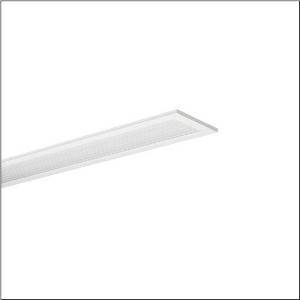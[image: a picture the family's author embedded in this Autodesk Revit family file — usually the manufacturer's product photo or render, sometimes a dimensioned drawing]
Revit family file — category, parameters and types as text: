
# Revit family: apollon_21_linear_51mq15wd2414
name_source: partatom
category: Lighting Fixtures
units: mm (PartAtom-declared; Revit-internal decimal feet)

## family parameters
Cut with Voids When Loaded = No
Host = Face
Light Source = No
Part Type = Normal
Room Calculation Point = No
Round Connector Dimension = Use Diameter
Shared = No

## types (1)
- Apollon 21 linear (1 x LED, 2520 lm, 17.4 W, 4000K)
    Apparent Load = 17 VA
    CIE Flux Codes = 66 89 97 100 100
    Color Rendering = 80
    Color Temperature = 4000K
    Default Elevation = 1800 mm
    Description = Apollon 21 linear, office luminaire, primary optical cover: micro prismatic cover, of PMMA, CAT 2 (L<= 3000cd/m²), light emission: direct distribution, primary light characteristic: symmetric, installation type: lay-in mounting, recessed, LED, rated luminous flux: 2.520lm, luminous efficacy: 145lm/W, light colour: 840, colour temperature: 4000K, control gear: DALI 2, Multilumen, with terminal, 5-pole, mains connection: 220..240V, AC/DC, 0/50..60Hz, rated input power: 17.4W, suitable for self-contained emergency lighting element 59MQE002602A with integrated self-test function according to EN 60598-2-22, housing, of aluminium, coated, traffic white (RAL 9016), module: M625, length: 1.245mm, width: 179mm, height: 55mm, housing upper side, of sheet steel, galvanised, protection rating (complete): IP20, protection rating (lamp compartment, on room side): IP50, insulation class (complete): insulation class II (safety insulation), certification: CE, ENEC, UKCA, impact resistance: IK03, permissible operating ambient temperature: -20..+45°C, standard: EN 60598-2-22, corresponds to IFS (International Featured Standards) requirements for safety and quality in the food industry, packaging unit: 1 piece
    Height = 0 mm  [stored 0 ft]
    Lamp = 1 x LED
    Lamp Light Flux = 2520 lm
    Lamp Power = 17.4 W
    Lamp count = 1
    Length = 1245 mm
    Luminous efficacy = 145 lm/W
    Manufacturer = Siteco
    ModVariant = No
    Model = 51MQ15WD2414
    Mounting Place = Ceiling
    Mounting Type = Recessed
    Number of Poles = 1
    OnlyDefault = Yes
    Power Factor = 1
    Product Name = Apollon 21 linear
    Product group = office luminaire | ceiling recessed
    ProductGroupID = 400
    Protection Class = Protection class II
    Protection Degree = IP 20
    RLX_Detail_Level = 1
    RLX_Emergency_Light_Flux = 0 lm
    RLX_Emergency_Type = 0
    RLX_Emergency_Type_DB = No
    RlxData = <blob elided: 12897 chars, md5=920b65da>
    Socket = socket
    Standby Power = 0 W
    System Light Flux = 2520 lm
    System Power = 17 W
    Type Comments = Product without accessories
    Type Image = l_1291018.jpg
    URL = http://relux.com
    VarID = ---
    Voltage = 0 V
    Weight = 0.00 kg
    Width = 179 mm

note: [stored X ft] marks values corroborated as IEEE doubles in the binary element streams (Revit-internal decimal feet)

## geometry (parser evidence)
native form markers: Sweep x10
no freeform markers — native parametric forms only
